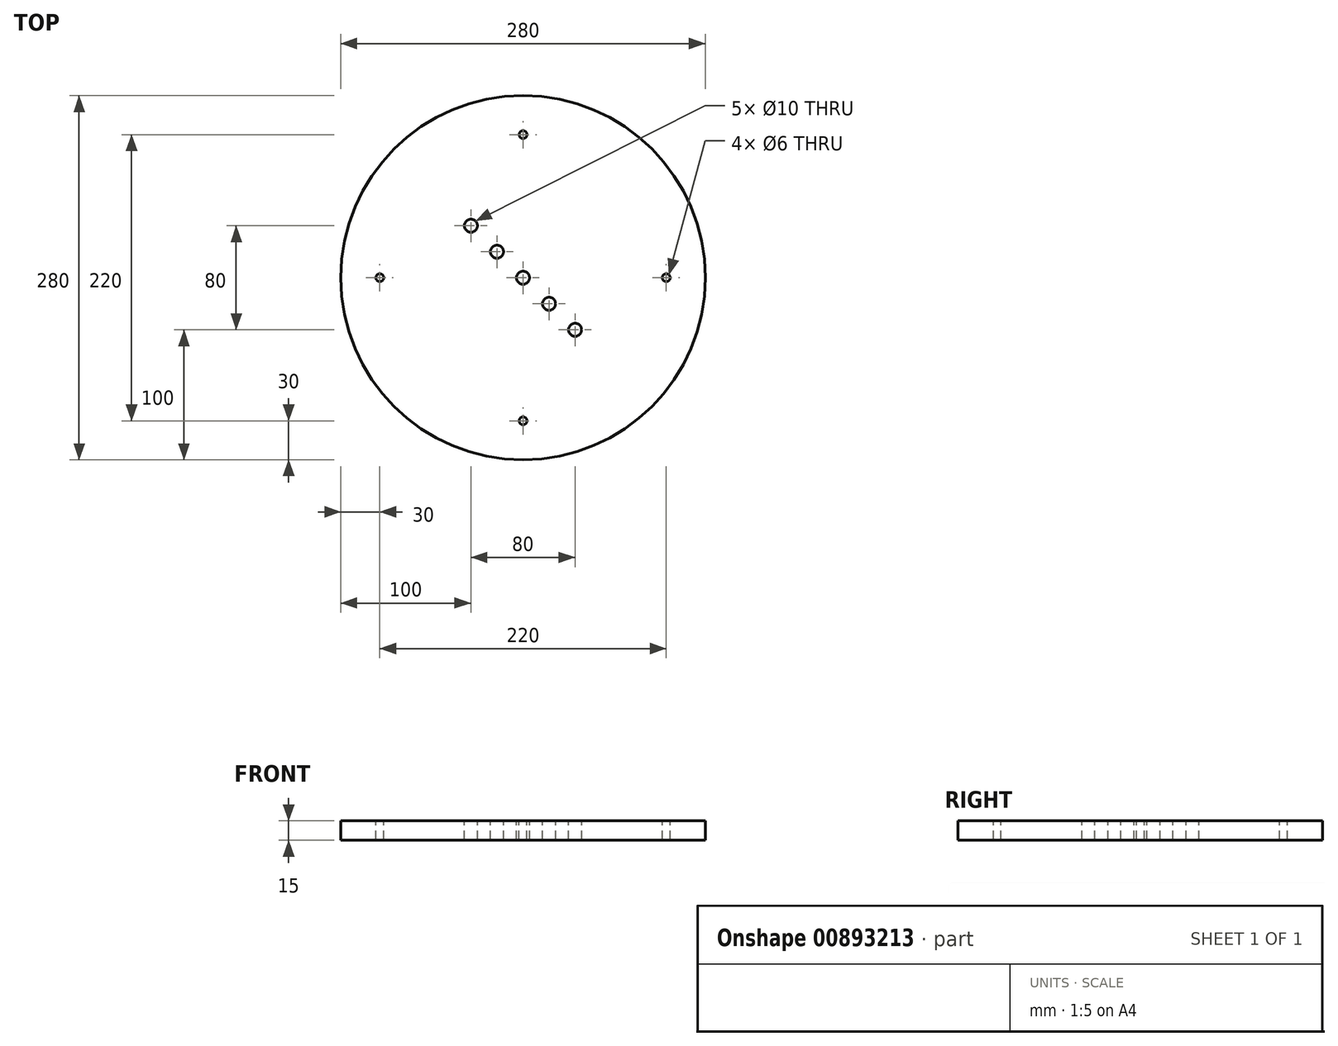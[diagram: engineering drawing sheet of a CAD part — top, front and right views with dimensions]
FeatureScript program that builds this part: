
annotation { "Feature Type Name" : "Feature", "Feature Type Description" : "" }
export const myFeature = defineFeature(function(context is Context, id is Id, definition is map)
    precondition{}
    {
        {
            var Q0;
            Q0=qCreatedBy(makeId("Top.planeOp"),FACE);
            var sketch = newSketch(context, id + "F0", { "sketchPlane" : qUnion([Q0])});
            skCircle(sketch, "E0", {"center": v(0, 0) * mm, "radius": 140 * mm});
            skSolve(sketch);
        }
        {
            var Q0;
            Q0=makeQuery(id+"F0.imprint","IMPRINT",FACE,{"disambiguationData":[TD([[makeQuery(id+"F0.imprint","IMPRINT",EDGE,{"derivedFrom":sQuery(id+"F0.wireOp",EDGE,"E0")}),1.0]])]});
            extrude(context, id + "F1", {"entities" : qUnion([Q0]), "depth" : 15 * mm, "offsetDistance" : 25 * mm});
        }
        {
            var Q0;
            Q0=makeQuery(id+"F1.opExtrude","CAP_FACE",FACE,{"disambiguationData":[OSD([sQuery(id+"F0.wireOp",EDGE,"E0")])],"isStart":false});
            var sketch = newSketch(context, id + "F2", { "sketchPlane" : qUnion([Q0])});
            skCircle(sketch, "E1", {"center": v(0, 0) * mm, "radius": 110 * mm});
            skCircle(sketch, "E2", {"center": v(0, 110) * mm, "radius": 3 * mm});
            skCircle(sketch, "E3", {"center": v(110, 0) * mm, "radius": 3 * mm});
            skCircle(sketch, "E4", {"center": v(0, -110) * mm, "radius": 3 * mm});
            skCircle(sketch, "E5", {"center": v(-110, 0) * mm, "radius": 3 * mm});
            skSolve(sketch);
        }
        {
            var Q0;
            {var subQ0=sQuery(id+"F2.wireOp",EDGE,"E5");var subQ1=sQuery(id+"F2.wireOp",EDGE,"E1");var subQ2=makeQuery(id+"F2.imprint","INTERSECT",VERTEX,{"disambiguationData":[OD(0.0)],"derivedFrom":[subQ1,subQ0]});Q0=makeQuery(id+"F2.imprint","IMPRINT",FACE,{"disambiguationData":[TD([[makeQuery(id+"F2.imprint","IMPRINT",EDGE,{"disambiguationData":[TD([[subQ2,-1.0]])],"derivedFrom":subQ1}),1.0]])]});}
            var Q1;
            {var subQ0=sQuery(id+"F2.wireOp",EDGE,"E5");var subQ1=sQuery(id+"F2.wireOp",EDGE,"E1");var subQ2=makeQuery(id+"F2.imprint","INTERSECT",VERTEX,{"disambiguationData":[OD(0.0)],"derivedFrom":[subQ1,subQ0]});Q1=makeQuery(id+"F2.imprint","IMPRINT",FACE,{"disambiguationData":[TD([[makeQuery(id+"F2.imprint","IMPRINT",EDGE,{"disambiguationData":[TD([[subQ2,-1.0]])],"derivedFrom":subQ1}),-1.0]])]});}
            var Q2;
            {var subQ0=sQuery(id+"F2.wireOp",EDGE,"E2");var subQ1=sQuery(id+"F2.wireOp",EDGE,"E1");var subQ2=makeQuery(id+"F2.imprint","INTERSECT",VERTEX,{"disambiguationData":[OD(0.0)],"derivedFrom":[subQ1,subQ0]});Q2=makeQuery(id+"F2.imprint","IMPRINT",FACE,{"disambiguationData":[TD([[makeQuery(id+"F2.imprint","IMPRINT",EDGE,{"disambiguationData":[TD([[subQ2,-1.0]])],"derivedFrom":subQ1}),-1.0]])]});}
            var Q3;
            {var subQ0=sQuery(id+"F2.wireOp",EDGE,"E2");var subQ1=sQuery(id+"F2.wireOp",EDGE,"E1");var subQ2=makeQuery(id+"F2.imprint","INTERSECT",VERTEX,{"disambiguationData":[OD(0.0)],"derivedFrom":[subQ1,subQ0]});Q3=makeQuery(id+"F2.imprint","IMPRINT",FACE,{"disambiguationData":[TD([[makeQuery(id+"F2.imprint","IMPRINT",EDGE,{"disambiguationData":[TD([[subQ2,-1.0]])],"derivedFrom":subQ1}),1.0]])]});}
            var Q4;
            {var subQ0=sQuery(id+"F2.wireOp",EDGE,"E4");var subQ1=sQuery(id+"F2.wireOp",EDGE,"E1");var subQ2=makeQuery(id+"F2.imprint","INTERSECT",VERTEX,{"disambiguationData":[OD(0.0)],"derivedFrom":[subQ1,subQ0]});Q4=makeQuery(id+"F2.imprint","IMPRINT",FACE,{"disambiguationData":[TD([[makeQuery(id+"F2.imprint","IMPRINT",EDGE,{"disambiguationData":[TD([[subQ2,-1.0]])],"derivedFrom":subQ1}),1.0]])]});}
            var Q5;
            {var subQ0=sQuery(id+"F2.wireOp",EDGE,"E4");var subQ1=sQuery(id+"F2.wireOp",EDGE,"E1");var subQ2=makeQuery(id+"F2.imprint","INTERSECT",VERTEX,{"disambiguationData":[OD(0.0)],"derivedFrom":[subQ1,subQ0]});Q5=makeQuery(id+"F2.imprint","IMPRINT",FACE,{"disambiguationData":[TD([[makeQuery(id+"F2.imprint","IMPRINT",EDGE,{"disambiguationData":[TD([[subQ2,-1.0]])],"derivedFrom":subQ1}),-1.0]])]});}
            var Q6;
            {var subQ0=sQuery(id+"F2.wireOp",EDGE,"E3");var subQ1=sQuery(id+"F2.wireOp",EDGE,"E1");var subQ2=makeQuery(id+"F2.imprint","INTERSECT",VERTEX,{"disambiguationData":[OD(0.0)],"derivedFrom":[subQ1,subQ0]});Q6=makeQuery(id+"F2.imprint","IMPRINT",FACE,{"disambiguationData":[TD([[makeQuery(id+"F2.imprint","IMPRINT",EDGE,{"disambiguationData":[TD([[subQ2,1.0]])],"derivedFrom":subQ1}),1.0]])]});}
            var Q7;
            {var subQ0=sQuery(id+"F2.wireOp",EDGE,"E3");var subQ1=sQuery(id+"F2.wireOp",EDGE,"E1");var subQ2=makeQuery(id+"F2.imprint","INTERSECT",VERTEX,{"disambiguationData":[OD(0.0)],"derivedFrom":[subQ1,subQ0]});Q7=makeQuery(id+"F2.imprint","IMPRINT",FACE,{"disambiguationData":[TD([[makeQuery(id+"F2.imprint","IMPRINT",EDGE,{"disambiguationData":[TD([[subQ2,1.0]])],"derivedFrom":subQ1}),-1.0]])]});}
            extrude(context, id + "F3", {"entities" : qUnion([Q0, Q1, Q2, Q3, Q4, Q5, Q6, Q7]), "operationType" : NewBodyOperationType.REMOVE, "endBound" : BoundingType.THROUGH_ALL, "oppositeDirection" : true, "depth" : 25 * mm, "offsetDistance" : 25 * mm});
        }
        {
            var Q0;
            Q0=makeQuery(id+"F1.opExtrude","CAP_FACE",FACE,{"disambiguationData":[OSD([sQuery(id+"F0.wireOp",EDGE,"E0")])],"isStart":false});
            var sketch = newSketch(context, id + "F4", { "sketchPlane" : qUnion([Q0])});
            skLineSegment(sketch, "E6", {"start": v(0, 0) * mm, "end": v(-66.73, 66.73) * mm});
            skLineSegment(sketch, "E7", {"start": v(0, 0) * mm, "end": v(53.58, -53.58) * mm});
            skCircle(sketch, "E8", {"center": v(-20, 20) * mm, "radius": 5 * mm});
            skCircle(sketch, "E9", {"center": v(-40, 40) * mm, "radius": 5 * mm});
            skCircle(sketch, "E10", {"center": v(20, -20) * mm, "radius": 5 * mm});
            skCircle(sketch, "E11", {"center": v(40, -40) * mm, "radius": 5 * mm});
            skCircle(sketch, "E12", {"center": v(0, 0) * mm, "radius": 5 * mm});
            skSolve(sketch);
        }
        {
            var Q0;
            Q0 = qSketchRegion(id + "F4", true);
            extrude(context, id + "F5", {"entities" : qUnion([Q0]), "operationType" : NewBodyOperationType.REMOVE, "endBound" : BoundingType.THROUGH_ALL, "oppositeDirection" : true, "depth" : 25 * mm, "offsetDistance" : 25 * mm});
        }
    });
